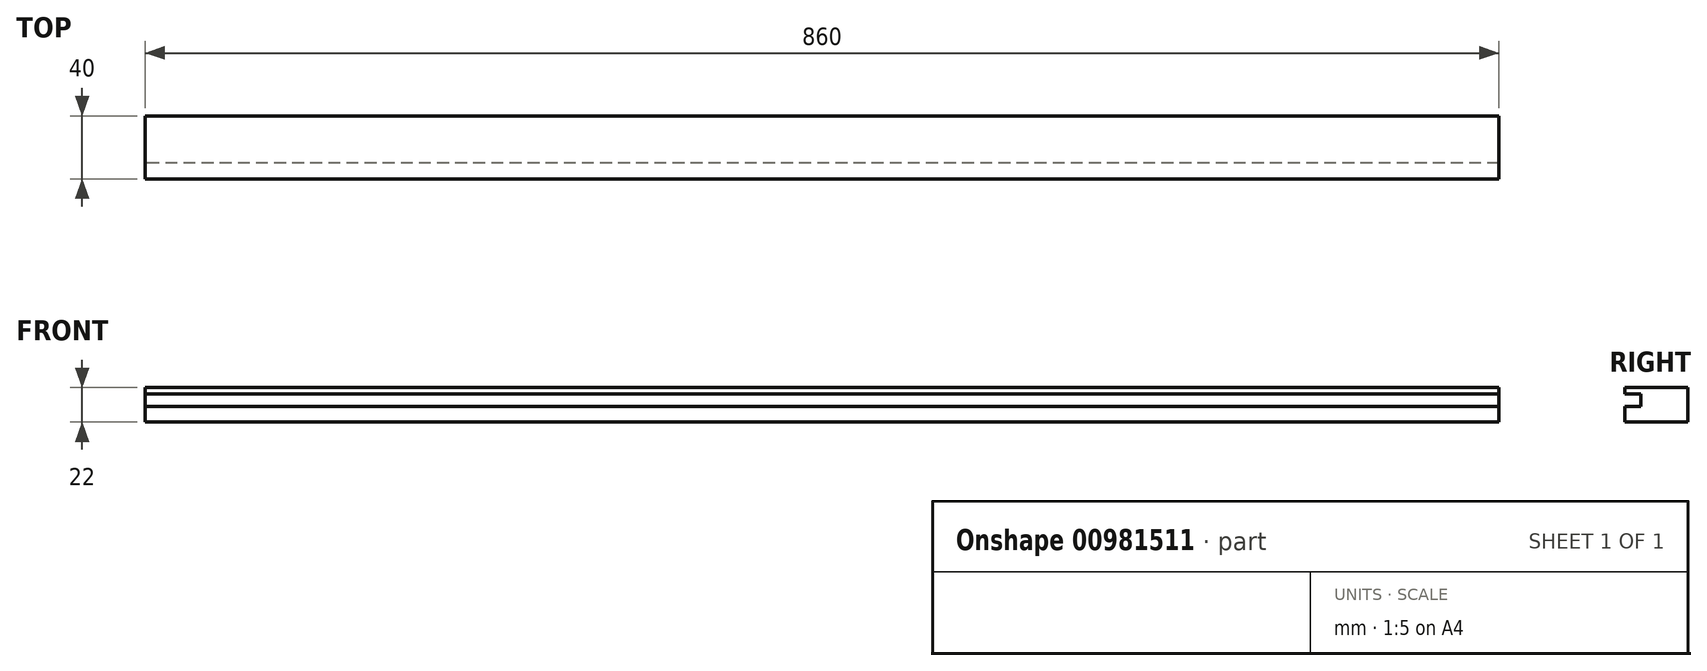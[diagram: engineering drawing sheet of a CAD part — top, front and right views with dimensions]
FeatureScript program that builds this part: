
annotation { "Feature Type Name" : "Feature", "Feature Type Description" : "" }
export const myFeature = defineFeature(function(context is Context, id is Id, definition is map)
    precondition{}
    {
        {
            var Q0;
            Q0=qCreatedBy(makeId("Right.planeOp"),FACE);
            var sketch = newSketch(context, id + "F0", { "sketchPlane" : qUnion([Q0])});
            skLineSegment(sketch, "E0.bottom", {"start": v(-30.65, 49.88) * mm, "end": v(9.35, 49.88) * mm});
            skLineSegment(sketch, "E0.top", {"start": v(-30.65, 27.88) * mm, "end": v(9.35, 27.88) * mm});
            skLineSegment(sketch, "E0.left", {"start": v(-30.65, 49.88) * mm, "end": v(-30.65, 27.88) * mm});
            skLineSegment(sketch, "E0.right", {"start": v(9.35, 49.88) * mm, "end": v(9.35, 27.88) * mm});
            skLineSegment(sketch, "E1.bottom", {"start": v(-30.65, 45.88) * mm, "end": v(-20.65, 45.88) * mm});
            skLineSegment(sketch, "E1.top", {"start": v(-30.65, 37.88) * mm, "end": v(-20.65, 37.88) * mm});
            skLineSegment(sketch, "E1.left", {"start": v(-30.65, 45.88) * mm, "end": v(-30.65, 37.88) * mm});
            skLineSegment(sketch, "E1.right", {"start": v(-20.65, 45.88) * mm, "end": v(-20.65, 37.88) * mm});
            skSolve(sketch);
        }
        {
            var Q0;
            {var subQ4=sQuery(id+"F0.wireOp",EDGE,"E0.bottom");Q0=makeQuery(id+"F0.imprint","IMPRINT",FACE,{"disambiguationData":[TD([[makeQuery(id+"F0.imprint","IMPRINT",EDGE,{"derivedFrom":subQ4}),-1.0]])]});}
            extrude(context, id + "F1", {"entities" : qUnion([Q0]), "depth" : 860 * mm, "offsetDistance" : 25 * mm});
        }
    });
